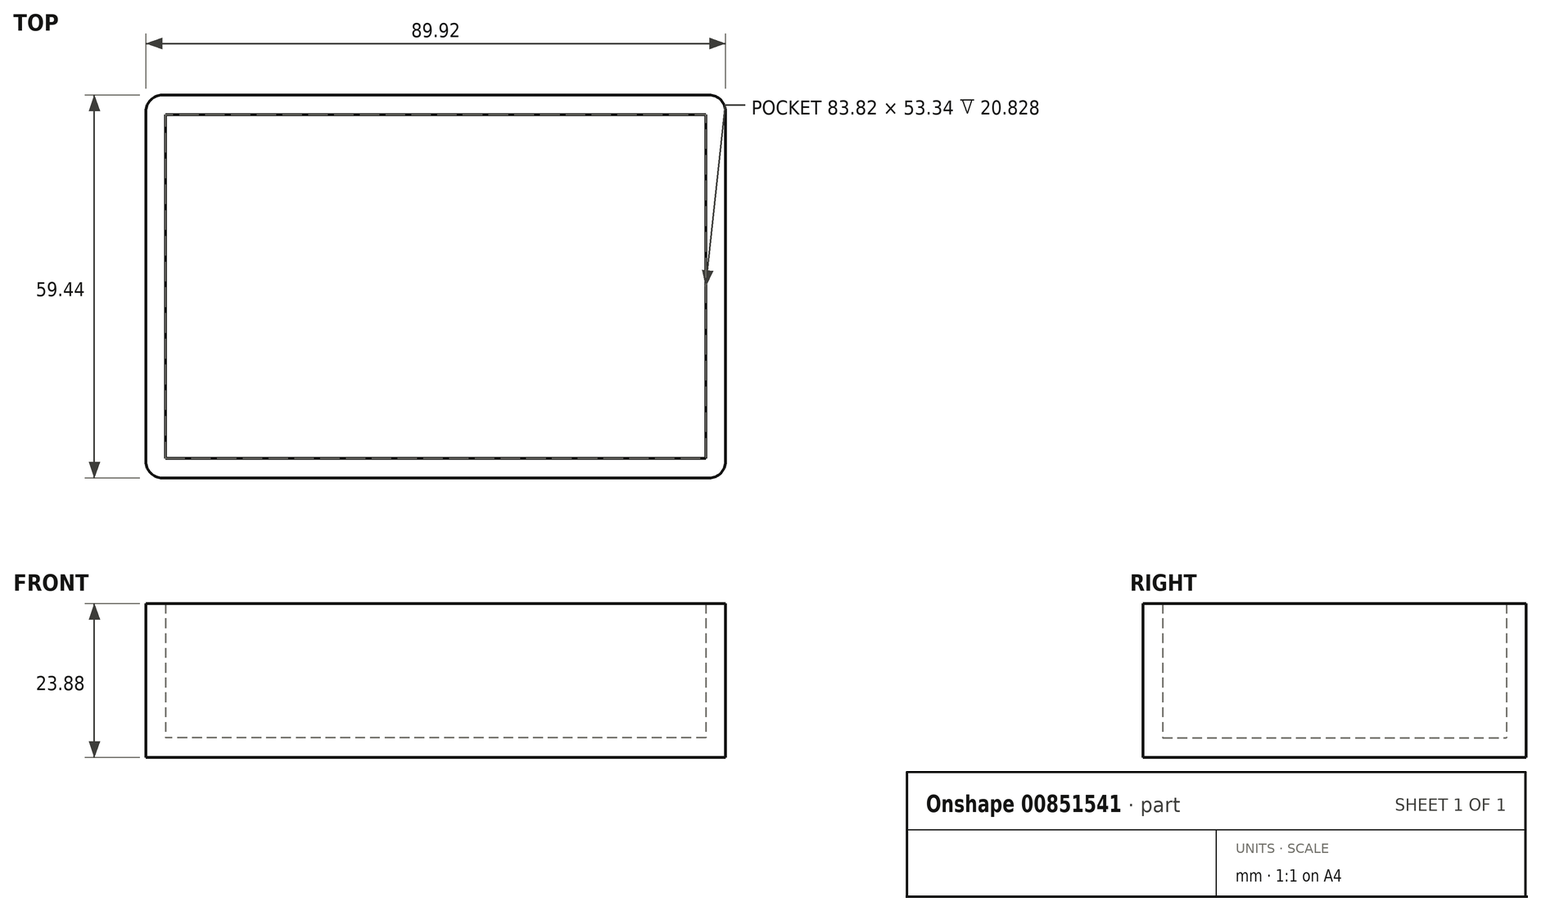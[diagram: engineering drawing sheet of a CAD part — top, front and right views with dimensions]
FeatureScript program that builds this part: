
annotation { "Feature Type Name" : "Feature", "Feature Type Description" : "" }
export const myFeature = defineFeature(function(context is Context, id is Id, definition is map)
    precondition{}
    {
        {
            var Q0;
            Q0=qCreatedBy(makeId("Top.planeOp"),FACE);
            var sketch = newSketch(context, id + "F0", { "sketchPlane" : qUnion([Q0])});
            skLineSegment(sketch, "E0.bottom", {"start": v(0, 0) * mm, "end": v(-89.92, 0) * mm});
            skLineSegment(sketch, "E0.top", {"start": v(0, 59.44) * mm, "end": v(-89.92, 59.44) * mm});
            skLineSegment(sketch, "E0.left", {"start": v(0, 0) * mm, "end": v(0, 59.44) * mm});
            skLineSegment(sketch, "E0.right", {"start": v(-89.92, 0) * mm, "end": v(-89.92, 59.44) * mm});
            skLineSegment(sketch, "E1.bottom", {"start": v(-3.05, 3.05) * mm, "end": v(-86.87, 3.05) * mm});
            skLineSegment(sketch, "E1.top", {"start": v(-3.05, 56.39) * mm, "end": v(-86.87, 56.39) * mm});
            skLineSegment(sketch, "E1.left", {"start": v(-3.05, 3.05) * mm, "end": v(-3.05, 56.39) * mm});
            skLineSegment(sketch, "E1.right", {"start": v(-86.87, 3.05) * mm, "end": v(-86.87, 56.39) * mm});
            skSolve(sketch);
        }
        {
            var Q0;
            Q0=makeQuery(id+"F0.imprint","IMPRINT",FACE,{"disambiguationData":[TD([[makeQuery(id+"F0.imprint","IMPRINT",EDGE,{"derivedFrom":sQuery(id+"F0.wireOp",EDGE,"E0.bottom")}),-1.0]])]});
            var Q1;
            Q1=makeQuery(id+"F0.imprint","IMPRINT",FACE,{"disambiguationData":[TD([[makeQuery(id+"F0.imprint","IMPRINT",EDGE,{"derivedFrom":sQuery(id+"F0.wireOp",EDGE,"E1.bottom")}),-1.0]])]});
            extrude(context, id + "F1", {"entities" : qUnion([Q0, Q1]), "depth" : -3.05 * mm, "offsetDistance" : 25.4 * mm});
        }
        {
            var Q0;
            Q0=makeQuery(id+"F0.imprint","IMPRINT",FACE,{"disambiguationData":[TD([[makeQuery(id+"F0.imprint","IMPRINT",EDGE,{"derivedFrom":sQuery(id+"F0.wireOp",EDGE,"E0.bottom")}),-1.0]])]});
            extrude(context, id + "F2", {"entities" : qUnion([Q0]), "operationType" : NewBodyOperationType.ADD, "depth" : 20.83 * mm, "offsetDistance" : 25.4 * mm});
        }
        {
            var Q0;
            {var subQ0=sQuery(id+"F0.wireOp",EDGE,"E0.left");var subQ1=sQuery(id+"F0.wireOp",EDGE,"E0.bottom");Q0=makeQuery(id+"F2.boolean.opBoolean","MERGE",EDGE,{"derivedFrom":[makeQuery(id+"F1.opExtrude","SWEPT_EDGE",EDGE,{"disambiguationData":[OSD([subQ1,subQ0])]}),makeQuery(id+"F2.opExtrude","SWEPT_EDGE",EDGE,{"disambiguationData":[OSD([subQ1,subQ0])]})]});}
            var Q1;
            {var subQ0=sQuery(id+"F0.wireOp",EDGE,"E0.left");var subQ1=sQuery(id+"F0.wireOp",EDGE,"E0.top");Q1=makeQuery(id+"F2.boolean.opBoolean","MERGE",EDGE,{"derivedFrom":[makeQuery(id+"F1.opExtrude","SWEPT_EDGE",EDGE,{"disambiguationData":[OSD([subQ1,subQ0])]}),makeQuery(id+"F2.opExtrude","SWEPT_EDGE",EDGE,{"disambiguationData":[OSD([subQ1,subQ0])]})]});}
            var Q2;
            {var subQ0=sQuery(id+"F0.wireOp",EDGE,"E0.right");var subQ1=sQuery(id+"F0.wireOp",EDGE,"E0.top");Q2=makeQuery(id+"F2.boolean.opBoolean","MERGE",EDGE,{"derivedFrom":[makeQuery(id+"F1.opExtrude","SWEPT_EDGE",EDGE,{"disambiguationData":[OSD([subQ1,subQ0])]}),makeQuery(id+"F2.opExtrude","SWEPT_EDGE",EDGE,{"disambiguationData":[OSD([subQ1,subQ0])]})]});}
            var Q3;
            {var subQ0=sQuery(id+"F0.wireOp",EDGE,"E0.right");var subQ1=sQuery(id+"F0.wireOp",EDGE,"E0.bottom");Q3=makeQuery(id+"F2.boolean.opBoolean","MERGE",EDGE,{"derivedFrom":[makeQuery(id+"F1.opExtrude","SWEPT_EDGE",EDGE,{"disambiguationData":[OSD([subQ1,subQ0])]}),makeQuery(id+"F2.opExtrude","SWEPT_EDGE",EDGE,{"disambiguationData":[OSD([subQ1,subQ0])]})]});}
            fillet(context, id + "F3", {"entities" : qUnion([Q0, Q1, Q2, Q3]), "radius" : 2.54 * mm, "tangentPropagation" : true, "allowEdgeOverflow" : false});
        }
    });
